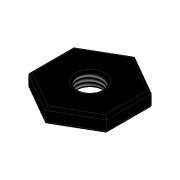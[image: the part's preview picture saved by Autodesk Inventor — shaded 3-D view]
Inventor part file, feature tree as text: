
AUTODESK INVENTOR PART (.ipt)
format: ipt  version: 2020 (Build 240168000, 168)  size: 117,248 bytes
history: native  units: mm
features: extrude x1, fillet x1, thread x1, sketch x1
ambient origin geometry x8: Origin, YZ Plane, XZ Plane, XY Plane, X Axis, Y Axis, Z Axis, Center Point
bodies: Solid1 (feature_tree)
feature tree (4):
  extrude  "Extrusion1"  Depth=0.5mm
  fillet  "Fillet1"  Radius=3.0mm
  thread  "Thread1"  [1 undecoded]
  sketch  "Sketch1"  dims[d0=7.9mm d1=5.0mm d2=3.0mm d3=0.0mm d4=0.5mm d5=2.0mm d6=0.0mm]
note: 1 required parameter value undecoded (feature->parameter linkage not recoverable at this tier; creation-order binding heuristic only, values carry confidence <= 0.55)
